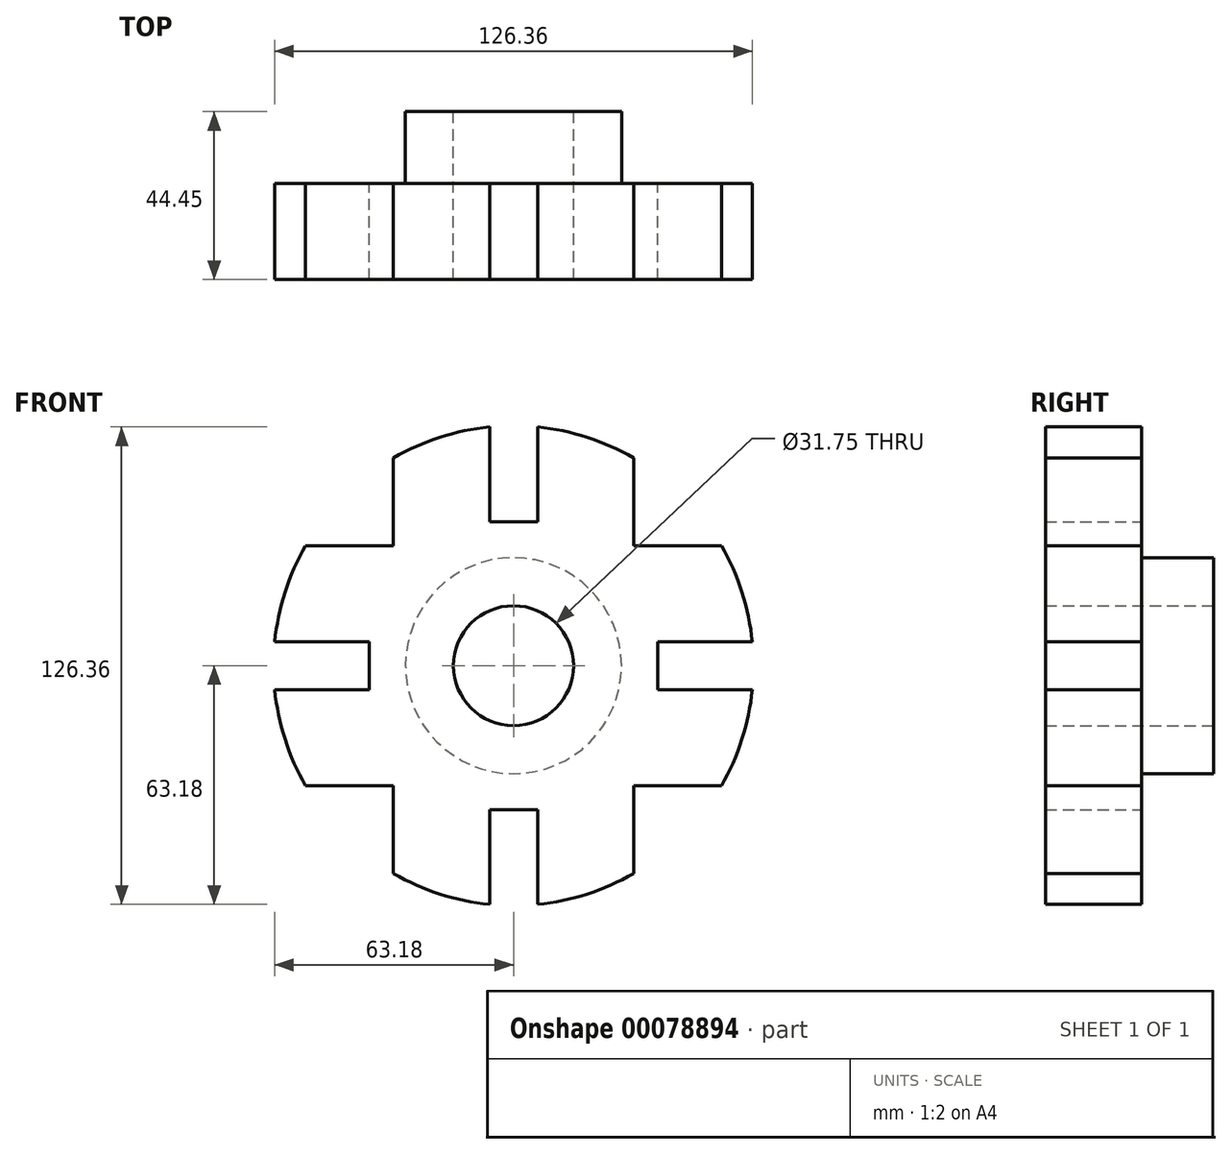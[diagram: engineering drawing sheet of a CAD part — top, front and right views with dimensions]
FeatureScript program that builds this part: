
annotation { "Feature Type Name" : "Feature", "Feature Type Description" : "" }
export const myFeature = defineFeature(function(context is Context, id is Id, definition is map)
    precondition{}
    {
        {
            var Q0;
            Q0=qCreatedBy(makeId("Front.planeOp"),FACE);
            var sketch = newSketch(context, id + "F0", { "sketchPlane" : qUnion([Q0])});
            skArc(sketch, "E0", {"start": v(63.18, 6.35) * mm, "mid": v(60.44, 19.49) * mm, "end": v(55, 31.75) * mm});
            skCircle(sketch, "E1", {"center": v(0, 0) * mm, "radius": 28.58 * mm});
            skCircle(sketch, "E2", {"center": v(0, 0) * mm, "radius": 15.88 * mm});
            skLineSegment(sketch, "E3", {"start": v(0, 63.5) * mm, "end": v(0, 0) * mm, "construction": true});
            skLineSegment(sketch, "E4", {"start": v(0, 38.1) * mm, "end": v(6.35, 38.1) * mm});
            skLineSegment(sketch, "E5", {"start": v(6.35, 38.1) * mm, "end": v(6.35, 63.18) * mm});
            skLineSegment(sketch, "E6", {"start": v(31.75, 55) * mm, "end": v(31.75, 31.75) * mm});
            skLineSegment(sketch, "E7", {"start": v(31.75, 31.75) * mm, "end": v(55, 31.75) * mm});
            skLineSegment(sketch, "E8", {"start": v(38.1, 0) * mm, "end": v(38.1, 6.35) * mm});
            skLineSegment(sketch, "E9", {"start": v(38.1, 6.35) * mm, "end": v(63.18, 6.35) * mm});
            skLineSegment(sketch, "E10.trimOffspring", {"start": v(0, 0) * mm, "end": v(63.5, 0) * mm, "construction": true});
            skArc(sketch, "E11.trimOffspring", {"start": v(31.75, 55) * mm, "mid": v(19.49, 60.44) * mm, "end": v(6.35, 63.18) * mm});
            skLineSegment(sketch, "E12.1.0", {"start": v(-55, 31.75) * mm, "end": v(-31.75, 31.75) * mm});
            skArc(sketch, "E12.1.1", {"start": v(-55, 31.75) * mm, "mid": v(-60.44, 19.49) * mm, "end": v(-63.18, 6.35) * mm});
            skLineSegment(sketch, "E12.1.2", {"start": v(-31.75, 31.75) * mm, "end": v(-31.75, 55) * mm});
            skLineSegment(sketch, "E12.1.3", {"start": v(-38.1, 6.35) * mm, "end": v(-63.18, 6.35) * mm});
            skLineSegment(sketch, "E12.1.4", {"start": v(-6.35, 38.1) * mm, "end": v(-6.35, 63.18) * mm});
            skArc(sketch, "E12.1.5", {"start": v(-6.35, 63.18) * mm, "mid": v(-19.49, 60.44) * mm, "end": v(-31.75, 55) * mm});
            skLineSegment(sketch, "E12.1.6", {"start": v(-38.1, 0) * mm, "end": v(-38.1, 6.35) * mm});
            skLineSegment(sketch, "E12.1.7", {"start": v(0, 38.1) * mm, "end": v(-6.35, 38.1) * mm});
            skLineSegment(sketch, "E12.2.0", {"start": v(-31.75, -55) * mm, "end": v(-31.75, -31.75) * mm});
            skArc(sketch, "E12.2.1", {"start": v(-31.75, -55) * mm, "mid": v(-19.49, -60.44) * mm, "end": v(-6.35, -63.18) * mm});
            skLineSegment(sketch, "E12.2.2", {"start": v(-31.75, -31.75) * mm, "end": v(-55, -31.75) * mm});
            skLineSegment(sketch, "E12.2.3", {"start": v(-6.35, -38.1) * mm, "end": v(-6.35, -63.18) * mm});
            skLineSegment(sketch, "E12.2.4", {"start": v(-38.1, -6.35) * mm, "end": v(-63.18, -6.35) * mm});
            skArc(sketch, "E12.2.5", {"start": v(-63.18, -6.35) * mm, "mid": v(-60.44, -19.49) * mm, "end": v(-55, -31.75) * mm});
            skLineSegment(sketch, "E12.2.6", {"start": v(0, -38.1) * mm, "end": v(-6.35, -38.1) * mm});
            skLineSegment(sketch, "E12.2.7", {"start": v(-38.1, 0) * mm, "end": v(-38.1, -6.35) * mm});
            skLineSegment(sketch, "E12.3.0", {"start": v(55, -31.75) * mm, "end": v(31.75, -31.75) * mm});
            skArc(sketch, "E12.3.1", {"start": v(55, -31.75) * mm, "mid": v(60.44, -19.49) * mm, "end": v(63.18, -6.35) * mm});
            skLineSegment(sketch, "E12.3.2", {"start": v(31.75, -31.75) * mm, "end": v(31.75, -55) * mm});
            skLineSegment(sketch, "E12.3.3", {"start": v(38.1, -6.35) * mm, "end": v(63.18, -6.35) * mm});
            skLineSegment(sketch, "E12.3.4", {"start": v(6.35, -38.1) * mm, "end": v(6.35, -63.18) * mm});
            skArc(sketch, "E12.3.5", {"start": v(6.35, -63.18) * mm, "mid": v(19.49, -60.44) * mm, "end": v(31.75, -55) * mm});
            skLineSegment(sketch, "E12.3.6", {"start": v(38.1, 0) * mm, "end": v(38.1, -6.35) * mm});
            skLineSegment(sketch, "E12.3.7", {"start": v(0, -38.1) * mm, "end": v(6.35, -38.1) * mm});
            skSolve(sketch);
        }
        {
            var Q0;
            Q0 = qSketchRegion(id + "F0", true);
            var Q1;
            Q1=makeQuery(id+"F0.imprint","IMPRINT",FACE,{"disambiguationData":[TD([[makeQuery(id+"F0.imprint","IMPRINT",EDGE,{"derivedFrom":sQuery(id+"F0.wireOp",EDGE,"E1")}),1.0]])]});
            extrude(context, id + "F1", {"entities" : qUnion([Q0, Q1]), "depth" : 25.4 * mm});
        }
        {
            var Q0;
            Q0=makeQuery(id+"F0.imprint","IMPRINT",FACE,{"disambiguationData":[TD([[makeQuery(id+"F0.imprint","IMPRINT",EDGE,{"derivedFrom":sQuery(id+"F0.wireOp",EDGE,"E1")}),1.0]])]});
            extrude(context, id + "F2", {"entities" : qUnion([Q0]), "operationType" : NewBodyOperationType.ADD, "oppositeDirection" : true, "depth" : 19.05 * mm});
        }
    });
